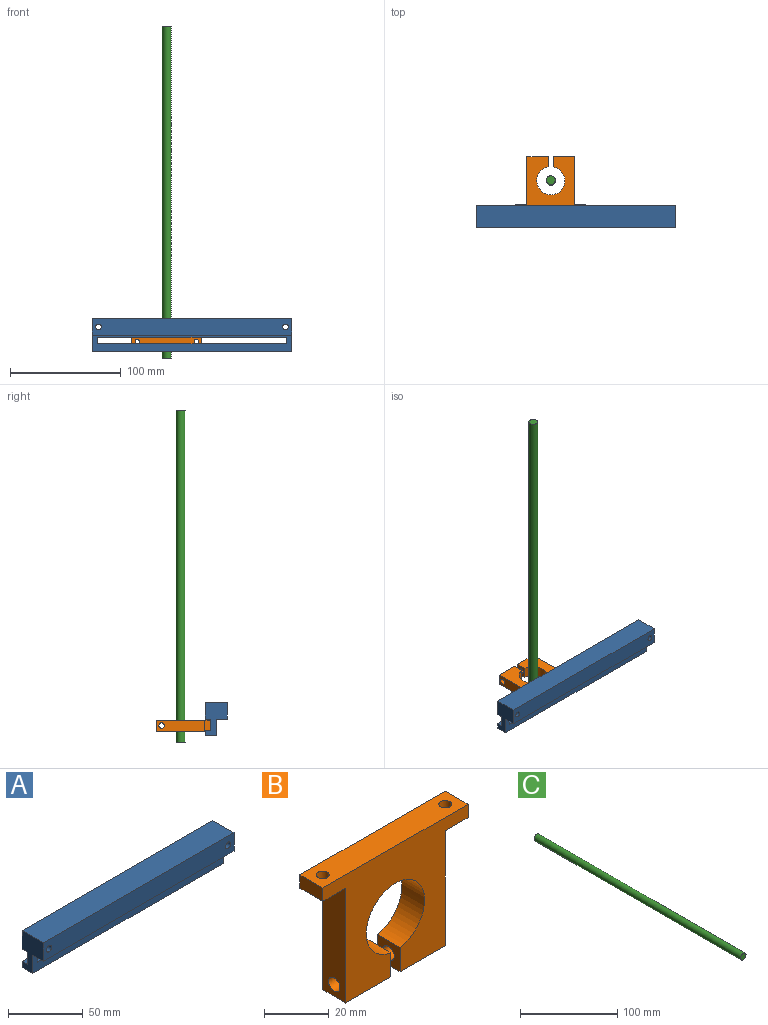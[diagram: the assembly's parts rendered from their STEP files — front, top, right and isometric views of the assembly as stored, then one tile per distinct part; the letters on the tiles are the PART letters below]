
ASSEMBLY  parts=3 mates=2
PART A: 18 faces, bbox 180x20x30 mm
  f0: plane 180x15mm, normal (0,-1,0), area 1676.5mm2, adj f3,f4,f5,f11,f14,f15,f16,f17
  f1: plane 180x10mm, normal (0,1,0), area 776.5mm2, adj f3,f4,f12,f13,f14,f15,f16,f17
  f2: plane 180x15mm, normal (0,1,0), area 2660.7mm2, adj f3,f4,f6,f7,f8,f12
  f3: plane 30x20mm, normal (1,0,0), area 400mm2, adj f0,f1,f2,f5,f6,f9,f10,f11
  f4: plane 30x20mm, normal (-1,0,0), area 400mm2, adj f0,f1,f2,f5,f6,f9,f10,f11
  f5: plane 180x10mm, normal (0,0,-1), area 1800mm2, adj f0,f3,f4,f10
  f6: plane 180x20mm, normal (0,0,1), area 3600mm2, adj f2,f3,f4,f9
  f7: cylinder r=2.5mm len=20mm, axis (0,1,0), area 314.2mm2, adj f2,f9
  f8: cylinder r=2.5mm len=20mm, axis (0,1,0), area 314.2mm2, adj f2,f9
  f9: plane 180x15mm, normal (0,-1,0), area 2660.7mm2, adj f3,f4,f6,f7,f8,f11
  f10: plane 180x5mm, normal (0,1,0), area 900mm2, adj f3,f4,f5,f13
  f11: plane 180x10mm, normal (0,0,-1), area 1800mm2, adj f0,f3,f4,f9
  f12: plane 180x5mm, normal (0,0,-1), area 900mm2, adj f1,f2,f3,f4
  f13: plane 180x5mm, normal (0,0,1), area 900mm2, adj f1,f3,f4,f10
  f14: plane 170.58x5mm, normal (0,0,1), area 852.9mm2, adj f0,f1,f15,f17
  f15: plane 6x5mm, normal (1,0,0), area 30mm2, adj f0,f1,f14,f16
  f16: plane 170.58x5mm, normal (0,0,-1), area 852.9mm2, adj f0,f1,f15,f17
  f17: plane 6x5mm, normal (-1,0,0), area 30mm2, adj f0,f1,f14,f16
PART B: 18 faces, bbox 63.5x10x48.5 mm
  f0: plane 43.48x10mm, normal (1,0,0), area 415.2mm2, adj f1,f11,f12,f13,f14
  f1: plane 10x10mm, normal (0,0,-1), area 87.4mm2, adj f0,f2,f12,f13,f17
  f2: plane 10x5mm, normal (1,0,0), area 50mm2, adj f1,f3,f12,f13
  f3: plane 63.48x10mm, normal (0,0,1), area 609.7mm2, adj f2,f4,f12,f13,f16,f17
  f4: plane 10x5mm, normal (-1,0,0), area 50mm2, adj f3,f5,f12,f13
  f5: plane 10x10mm, normal (0,0,-1), area 87.4mm2, adj f4,f6,f12,f13,f16
  f6: plane 43.48x10mm, normal (-1,0,0), area 415.2mm2, adj f5,f7,f12,f13,f15
  f7: plane 19.74x10mm, normal (0,0,-1), area 197.4mm2, adj f6,f8,f12,f13
  f8: plane 10x9.16mm, normal (1,0,0), area 71.9mm2, adj f7,f9,f12,f13,f15
  f9: cylinder r=12.74mm len=25.48mm, axis (0,1,0), area 760.3mm2, adj f8,f10,f12,f13
  f10: plane 10x9.16mm, normal (-1,0,0), area 71.9mm2, adj f9,f11,f12,f13,f14
  f11: plane 19.74x10mm, normal (0,0,-1), area 197.4mm2, adj f0,f10,f12,f13
  f12: plane 63.48x48.48mm, normal (0,-1,0), area 1661.8mm2, adj f0,f1,f2,f3,f4,f5,f6,f7
  f13: plane 63.48x48.48mm, normal (0,1,0), area 1661.8mm2, adj f0,f1,f2,f3,f4,f5,f6,f7
  f14: cylinder r=2.5mm len=19.74mm, axis (-1,0,0), area 310.1mm2, adj f0,f10
  f15: cylinder r=2.5mm len=19.74mm, axis (-1,0,0), area 310.1mm2, adj f6,f8
  f16: cylinder r=2mm len=5mm, axis (0,0,-1), area 62.8mm2, adj f3,f5
  f17: cylinder r=2mm len=5mm, axis (0,0,-1), area 62.8mm2, adj f1,f3
PART C: 3 faces, bbox 8x300x8 mm
  f0: cylinder r=4mm len=300mm, axis (0,1,0), area 7539.8mm2, adj f1,f2
  f1: plane 8x8mm, normal (0,-1,0), area 50.3mm2, adj f0
  f2: plane 8x8mm, normal (0,1,0), area 50.3mm2, adj f0
PLACE A t=(-84.49,-179.65,-36.57)mm
PLACE B rot(axis=(0,0.71,-0.71),180deg) t=(-107.21,-157.63,-47.43)mm
PLACE C rot(axis=(0,0.71,-0.71),180deg) t=(-107.21,-157.63,-57.22)mm
MATE parallel B.f17 <-> A.f1  axis (0,-1,0) through (-133.95,-184.37,-42.43)mm
MATE slider C.f0 <-> B.f9  axis (0,0,-1) through (-107.21,-157.63,92.78)mm
